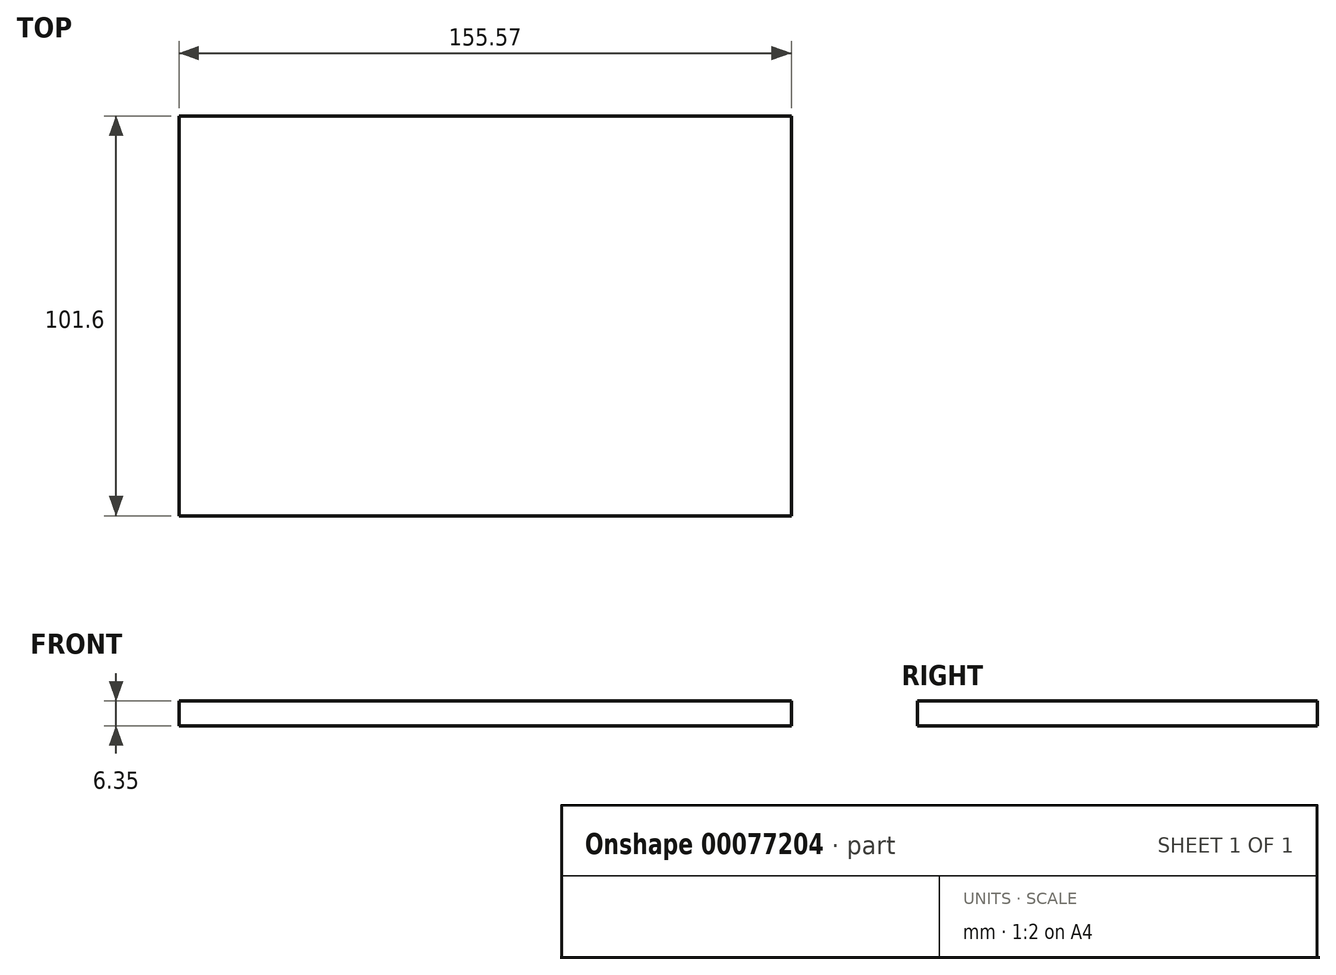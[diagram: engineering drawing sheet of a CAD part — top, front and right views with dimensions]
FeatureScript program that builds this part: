
annotation { "Feature Type Name" : "Feature", "Feature Type Description" : "" }
export const myFeature = defineFeature(function(context is Context, id is Id, definition is map)
    precondition{}
    {
        {
            var Q0;
            Q0=qCreatedBy(makeId("Top.planeOp"),FACE);
            var sketch = newSketch(context, id + "F0", { "sketchPlane" : qUnion([Q0])});
            skLineSegment(sketch, "E0.bottom", {"start": v(0, 0) * mm, "end": v(-155.58, 0) * mm});
            skLineSegment(sketch, "E0.top", {"start": v(0, -101.6) * mm, "end": v(-155.57, -101.6) * mm});
            skLineSegment(sketch, "E0.left", {"start": v(0, 0) * mm, "end": v(0, -101.6) * mm});
            skLineSegment(sketch, "E0.right", {"start": v(-155.58, 0) * mm, "end": v(-155.58, -101.6) * mm});
            skSolve(sketch);
        }
        {
            var Q0;
            Q0=makeQuery(id+"F0.imprint","IMPRINT",FACE,{"disambiguationData":[TD([[makeQuery(id+"F0.imprint","IMPRINT",EDGE,{"derivedFrom":sQuery(id+"F0.wireOp",EDGE,"E0.bottom")}),1.0]])]});
            extrude(context, id + "F1", {"entities" : qUnion([Q0]), "depth" : 6.35 * mm});
        }
    });
